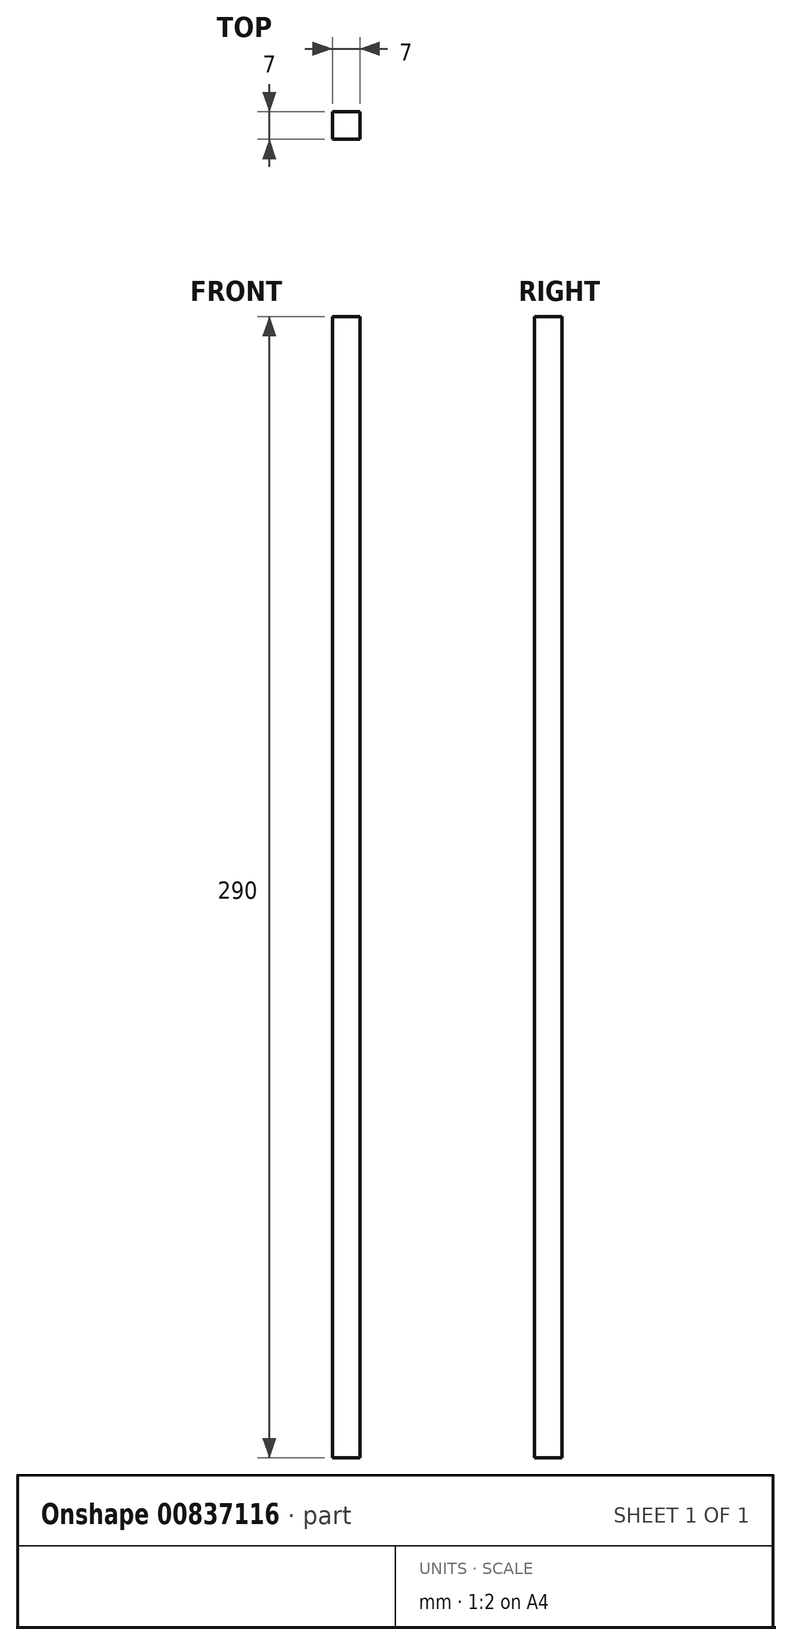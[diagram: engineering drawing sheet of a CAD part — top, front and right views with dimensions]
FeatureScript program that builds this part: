
annotation { "Feature Type Name" : "Feature", "Feature Type Description" : "" }
export const myFeature = defineFeature(function(context is Context, id is Id, definition is map)
    precondition{}
    {
        {
            var Q0;
            Q0=qCreatedBy(makeId("Top.planeOp"),FACE);
            var sketch = newSketch(context, id + "F0", { "sketchPlane" : qUnion([Q0])});
            skLineSegment(sketch, "E0.bottom", {"start": v(0, 0) * mm, "end": v(7, 0) * mm});
            skLineSegment(sketch, "E0.top", {"start": v(0, 7) * mm, "end": v(7, 7) * mm});
            skLineSegment(sketch, "E0.left", {"start": v(0, 0) * mm, "end": v(0, 7) * mm});
            skLineSegment(sketch, "E0.right", {"start": v(7, 0) * mm, "end": v(7, 7) * mm});
            skSolve(sketch);
        }
        {
            var Q0;
            Q0 = qSketchRegion(id + "F0", true);
            extrude(context, id + "F1", {"entities" : qUnion([Q0]), "depth" : 290 * mm, "offsetDistance" : 25 * mm});
        }
    });
